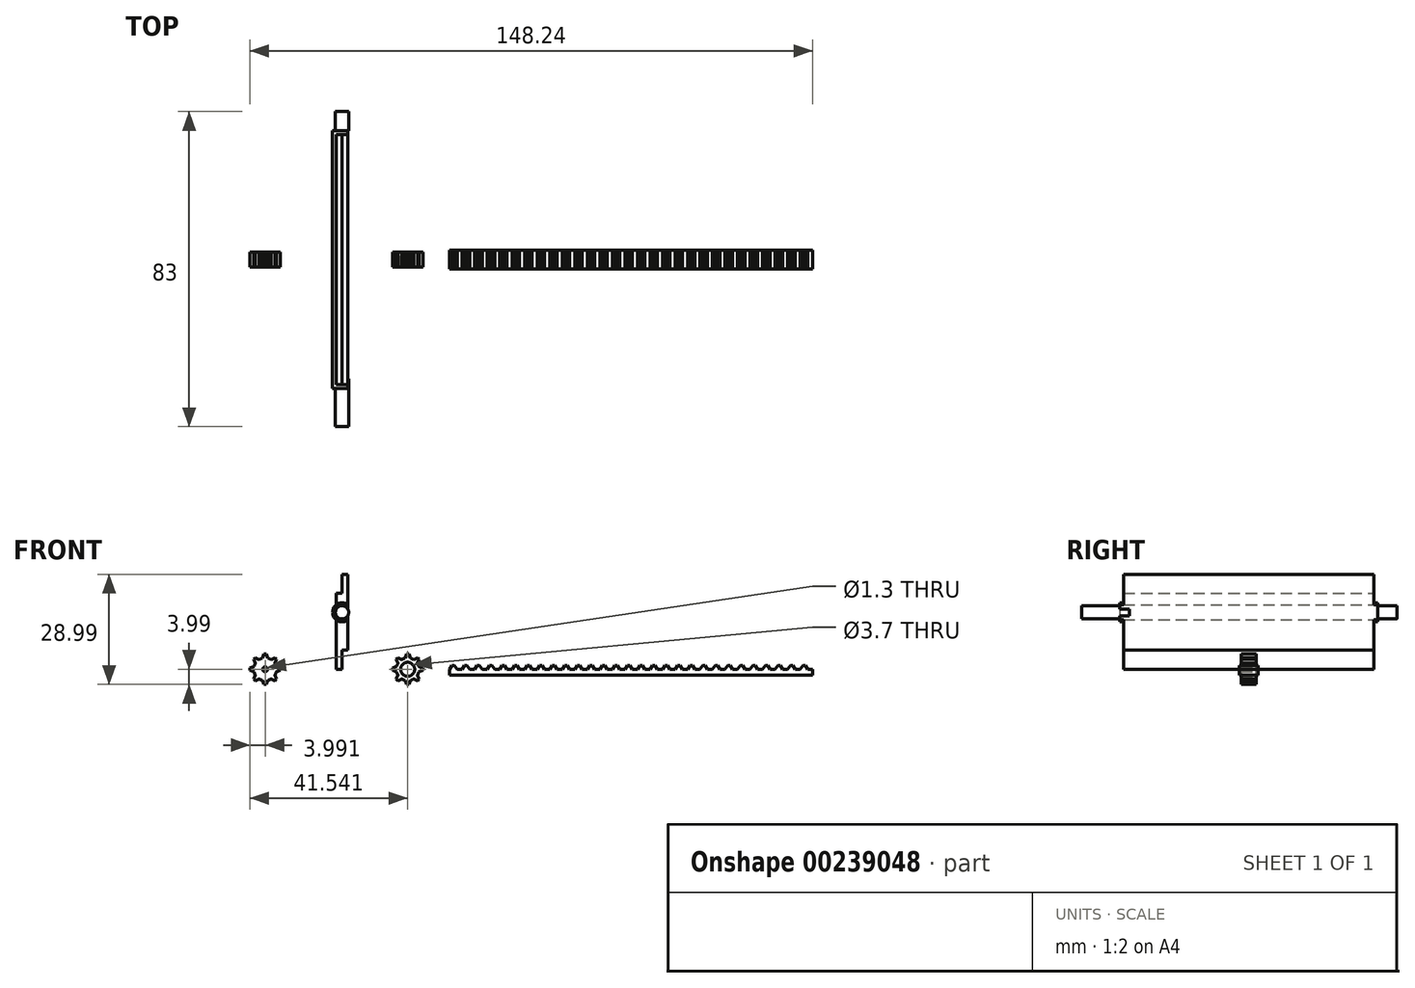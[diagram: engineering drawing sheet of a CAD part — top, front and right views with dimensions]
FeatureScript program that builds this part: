
annotation { "Feature Type Name" : "Feature", "Feature Type Description" : "" }
export const myFeature = defineFeature(function(context is Context, id is Id, definition is map)
    precondition{}
    {
        {
            var Q0;
            Q0=qCreatedBy(makeId("Front.planeOp"),FACE);
            var sketch = newSketch(context, id + "F0", { "sketchPlane" : qUnion([Q0])});
            skLineSegment(sketch, "E0", {"start": v(0, 0) * mm, "end": v(0, 20) * mm});
            skLineSegment(sketch, "E1", {"start": v(0, 20) * mm, "end": v(1.5, 20) * mm});
            skLineSegment(sketch, "E2", {"start": v(1.5, 20) * mm, "end": v(1.5, 25) * mm});
            skLineSegment(sketch, "E3", {"start": v(1.5, 25) * mm, "end": v(3, 25) * mm});
            skLineSegment(sketch, "E4", {"start": v(3, 25) * mm, "end": v(3, 5) * mm});
            skLineSegment(sketch, "E5", {"start": v(3, 5) * mm, "end": v(1.5, 5) * mm});
            skLineSegment(sketch, "E6", {"start": v(1.5, 5) * mm, "end": v(1.5, 0) * mm});
            skLineSegment(sketch, "E7", {"start": v(1.5, 0) * mm, "end": v(0, 0) * mm});
            skCircle(sketch, "E8", {"center": v(1.5, 15) * mm, "radius": 2.5 * mm});
            skSolve(sketch);
        }
        {
            var Q0;
            {var subQ1=sQuery(id+"F0.wireOp",EDGE,"E1");Q0=makeQuery(id+"F0.imprint","IMPRINT",FACE,{"disambiguationData":[TD([[makeQuery(id+"F0.imprint","IMPRINT",EDGE,{"derivedFrom":subQ1}),-1.0]])]});}
            var Q1;
            {var subQ0=sQuery(id+"F0.wireOp",EDGE,"E5");Q1=makeQuery(id+"F0.imprint","IMPRINT",FACE,{"disambiguationData":[TD([[makeQuery(id+"F0.imprint","IMPRINT",EDGE,{"derivedFrom":subQ0}),-1.0]])]});}
            var Q2;
            {var subQ0=sQuery(id+"F0.wireOp",EDGE,"E8");var subQ1=sQuery(id+"F0.wireOp",EDGE,"E0");var subQ2=makeQuery(id+"F0.imprint","INTERSECT",VERTEX,{"disambiguationData":[OD(0.0)],"derivedFrom":[subQ1,subQ0]});Q2=makeQuery(id+"F0.imprint","IMPRINT",FACE,{"disambiguationData":[TD([[makeQuery(id+"F0.imprint","IMPRINT",EDGE,{"disambiguationData":[TD([[subQ2,-1.0]])],"derivedFrom":subQ1}),-1.0]])]});}
            extrude(context, id + "F1", {"entities" : qUnion([Q0, Q1, Q2]), "endBound" : BoundingType.SYMMETRIC, "depth" : 66 * mm});
        }
        {
            var Q0;
            {var subQ0=sQuery(id+"F0.wireOp",EDGE,"E8");var subQ1=sQuery(id+"F0.wireOp",EDGE,"E0");var subQ2=makeQuery(id+"F0.imprint","INTERSECT",VERTEX,{"disambiguationData":[OD(0.0)],"derivedFrom":[subQ1,subQ0]});Q0=makeQuery(id+"F0.imprint","IMPRINT",FACE,{"disambiguationData":[TD([[makeQuery(id+"F0.imprint","IMPRINT",EDGE,{"disambiguationData":[TD([[subQ2,-1.0]])],"derivedFrom":subQ1}),-1.0]])]});}
            var Q1;
            {var subQ0=sQuery(id+"F0.wireOp",EDGE,"E8");var subQ1=sQuery(id+"F0.wireOp",EDGE,"E0");var subQ2=makeQuery(id+"F0.imprint","INTERSECT",VERTEX,{"disambiguationData":[OD(0.0)],"derivedFrom":[subQ1,subQ0]});Q1=makeQuery(id+"F0.imprint","IMPRINT",FACE,{"disambiguationData":[TD([[makeQuery(id+"F0.imprint","IMPRINT",EDGE,{"disambiguationData":[TD([[subQ2,-1.0]])],"derivedFrom":subQ1}),1.0]])]});}
            var Q2;
            {var subQ0=sQuery(id+"F0.wireOp",EDGE,"E8");var subQ1=sQuery(id+"F0.wireOp",EDGE,"E4");var subQ2=makeQuery(id+"F0.imprint","INTERSECT",VERTEX,{"disambiguationData":[OD(0.0)],"derivedFrom":[subQ1,subQ0]});Q2=makeQuery(id+"F0.imprint","IMPRINT",FACE,{"disambiguationData":[TD([[makeQuery(id+"F0.imprint","IMPRINT",EDGE,{"disambiguationData":[TD([[subQ2,-1.0]])],"derivedFrom":subQ1}),1.0]])]});}
            extrude(context, id + "F2", {"entities" : qUnion([Q0, Q1, Q2]), "operationType" : NewBodyOperationType.ADD, "depth" : 34 * mm, "hasSecondDirection" : true, "secondDirectionOppositeDirection" : true, "secondDirectionDepth" : 34 * mm});
        }
        {
            var Q0;
            Q0=makeQuery(id+"F2.opExtrude","CAP_FACE",FACE,{"disambiguationData":[OSD([sQuery(id+"F0.wireOp",EDGE,"E8")])],"isStart":false});
            var sketch = newSketch(context, id + "F3", { "sketchPlane" : qUnion([Q0])});
            skCircle(sketch, "E9", {"center": v(1.5, 15) * mm, "radius": 1.75 * mm});
            skSolve(sketch);
        }
        {
            var Q0;
            Q0 = qSketchRegion(id + "F3", true);
            extrude(context, id + "F4", {"entities" : qUnion([Q0]), "operationType" : NewBodyOperationType.ADD, "depth" : 10 * mm});
        }
        {
            var Q0;
            Q0=makeQuery(id+"F2.opExtrude","CAP_FACE",FACE,{"disambiguationData":[OSD([sQuery(id+"F0.wireOp",EDGE,"E8")])],"isStart":true});
            var sketch = newSketch(context, id + "F5", { "sketchPlane" : qUnion([Q0])});
            skCircle(sketch, "E10", {"center": v(-1.5, 15) * mm, "radius": 1.75 * mm});
            skSolve(sketch);
        }
        {
            var Q0;
            Q0 = qSketchRegion(id + "F5", true);
            extrude(context, id + "F6", {"entities" : qUnion([Q0]), "operationType" : NewBodyOperationType.ADD, "depth" : 5 * mm});
        }
        {
            var Q0;
            Q0=qCreatedBy(makeId("Front.planeOp"),FACE);
            var sketch = newSketch(context, id + "F7", { "sketchPlane" : qUnion([Q0])});
            skCircle(sketch, "E11", {"center": v(18.78, 0) * mm, "radius": 1.85 * mm});
            skArc(sketch, "E12", {"start": v(16.22, 1.57) * mm, "mid": v(16, 1.15) * mm, "end": v(15.86, 0.7) * mm});
            skCircle(sketch, "E13", {"center": v(18.78, 0) * mm, "radius": 4 * mm, "construction": true});
            skLineSegment(sketch, "E14", {"start": v(18.78, 0) * mm, "end": v(18.78, 4) * mm, "construction": true});
            skLineSegment(sketch, "E15", {"start": v(19.08, 3.99) * mm, "end": v(19.48, 2.92) * mm});
            skLineSegment(sketch, "E16.MirrorCS", {"start": v(18.48, 3.99) * mm, "end": v(18.08, 2.92) * mm});
            skLineSegment(sketch, "E17", {"start": v(18.48, 3.99) * mm, "end": v(19.08, 3.99) * mm});
            skLineSegment(sketch, "E18.1.0", {"start": v(21.39, 3.03) * mm, "end": v(20.35, 2.56) * mm});
            skLineSegment(sketch, "E18.1.1", {"start": v(21.39, 3.03) * mm, "end": v(21.81, 2.6) * mm});
            skLineSegment(sketch, "E18.1.2", {"start": v(21.81, 2.6) * mm, "end": v(21.34, 1.57) * mm});
            skLineSegment(sketch, "E18.2.0", {"start": v(22.77, 0.3) * mm, "end": v(21.7, 0.7) * mm});
            skLineSegment(sketch, "E18.2.1", {"start": v(22.77, 0.3) * mm, "end": v(22.77, -0.3) * mm});
            skLineSegment(sketch, "E18.2.2", {"start": v(22.77, -0.3) * mm, "end": v(21.7, -0.7) * mm});
            skLineSegment(sketch, "E18.3.0", {"start": v(21.81, -2.6) * mm, "end": v(21.34, -1.57) * mm});
            skLineSegment(sketch, "E18.3.1", {"start": v(21.81, -2.6) * mm, "end": v(21.39, -3.03) * mm});
            skLineSegment(sketch, "E18.3.2", {"start": v(21.39, -3.03) * mm, "end": v(20.35, -2.56) * mm});
            skLineSegment(sketch, "E18.4.0", {"start": v(19.08, -3.99) * mm, "end": v(19.48, -2.92) * mm});
            skLineSegment(sketch, "E18.4.1", {"start": v(19.08, -3.99) * mm, "end": v(18.48, -3.99) * mm});
            skLineSegment(sketch, "E18.4.2", {"start": v(18.48, -3.99) * mm, "end": v(18.08, -2.92) * mm});
            skLineSegment(sketch, "E18.5.0", {"start": v(16.17, -3.03) * mm, "end": v(17.21, -2.56) * mm});
            skLineSegment(sketch, "E18.5.1", {"start": v(16.17, -3.03) * mm, "end": v(15.75, -2.6) * mm});
            skLineSegment(sketch, "E18.5.2", {"start": v(15.75, -2.6) * mm, "end": v(16.22, -1.57) * mm});
            skLineSegment(sketch, "E18.6.0", {"start": v(14.8, -0.3) * mm, "end": v(15.86, -0.7) * mm});
            skLineSegment(sketch, "E18.6.1", {"start": v(14.8, -0.3) * mm, "end": v(14.8, 0.3) * mm});
            skLineSegment(sketch, "E18.6.2", {"start": v(14.8, 0.3) * mm, "end": v(15.86, 0.7) * mm});
            skLineSegment(sketch, "E18.7.0", {"start": v(15.75, 2.6) * mm, "end": v(16.22, 1.57) * mm});
            skLineSegment(sketch, "E18.7.1", {"start": v(15.75, 2.6) * mm, "end": v(16.17, 3.03) * mm});
            skLineSegment(sketch, "E18.7.2", {"start": v(16.17, 3.03) * mm, "end": v(17.21, 2.56) * mm});
            skLineSegment(sketch, "E18.anchor1", {"start": v(18.78, 0) * mm, "end": v(18.08, 2.92) * mm, "construction": true});
            skLineSegment(sketch, "E18.anchor2", {"start": v(18.78, 0) * mm, "end": v(16.22, 1.57) * mm, "construction": true});
            skLineSegment(sketch, "E19", {"start": v(31.78, 0) * mm, "end": v(31.08, 1) * mm});
            skLineSegment(sketch, "E20", {"start": v(31.08, 1) * mm, "end": v(30.48, 1) * mm});
            skLineSegment(sketch, "E21", {"start": v(30.48, 1) * mm, "end": v(29.78, 0) * mm});
            skLineSegment(sketch, "E22", {"start": v(31.78, 0) * mm, "end": v(33.08, 0) * mm});
            skLineSegment(sketch, "E23.1.0.0", {"start": v(33.78, 1) * mm, "end": v(33.08, 0) * mm});
            skLineSegment(sketch, "E23.1.0.1", {"start": v(34.38, 1) * mm, "end": v(33.78, 1) * mm});
            skLineSegment(sketch, "E23.1.0.2", {"start": v(35.08, 0) * mm, "end": v(34.38, 1) * mm});
            skLineSegment(sketch, "E23.1.0.3", {"start": v(35.08, 0) * mm, "end": v(36.38, 0) * mm});
            skLineSegment(sketch, "E23.2.0.0", {"start": v(37.08, 1) * mm, "end": v(36.38, 0) * mm});
            skLineSegment(sketch, "E23.2.0.1", {"start": v(37.68, 1) * mm, "end": v(37.08, 1) * mm});
            skLineSegment(sketch, "E23.2.0.2", {"start": v(38.38, 0) * mm, "end": v(37.68, 1) * mm});
            skLineSegment(sketch, "E23.2.0.3", {"start": v(38.38, 0) * mm, "end": v(39.68, 0) * mm});
            skLineSegment(sketch, "E23.3.0.0", {"start": v(40.38, 1) * mm, "end": v(39.68, 0) * mm});
            skLineSegment(sketch, "E23.3.0.1", {"start": v(40.98, 1) * mm, "end": v(40.38, 1) * mm});
            skLineSegment(sketch, "E23.3.0.2", {"start": v(41.68, 0) * mm, "end": v(40.98, 1) * mm});
            skLineSegment(sketch, "E23.3.0.3", {"start": v(41.68, 0) * mm, "end": v(42.98, 0) * mm});
            skLineSegment(sketch, "E23.4.0.0", {"start": v(43.68, 1) * mm, "end": v(42.98, 0) * mm});
            skLineSegment(sketch, "E23.4.0.1", {"start": v(44.28, 1) * mm, "end": v(43.68, 1) * mm});
            skLineSegment(sketch, "E23.4.0.2", {"start": v(44.98, 0) * mm, "end": v(44.28, 1) * mm});
            skLineSegment(sketch, "E23.4.0.3", {"start": v(44.98, 0) * mm, "end": v(46.28, 0) * mm});
            skLineSegment(sketch, "E23.5.0.0", {"start": v(46.98, 1) * mm, "end": v(46.28, 0) * mm});
            skLineSegment(sketch, "E23.5.0.1", {"start": v(47.58, 1) * mm, "end": v(46.98, 1) * mm});
            skLineSegment(sketch, "E23.5.0.2", {"start": v(48.28, 0) * mm, "end": v(47.58, 1) * mm});
            skLineSegment(sketch, "E23.5.0.3", {"start": v(48.28, 0) * mm, "end": v(49.58, 0) * mm});
            skLineSegment(sketch, "E23.6.0.0", {"start": v(50.28, 1) * mm, "end": v(49.58, 0) * mm});
            skLineSegment(sketch, "E23.6.0.1", {"start": v(50.88, 1) * mm, "end": v(50.28, 1) * mm});
            skLineSegment(sketch, "E23.6.0.2", {"start": v(51.58, 0) * mm, "end": v(50.88, 1) * mm});
            skLineSegment(sketch, "E23.6.0.3", {"start": v(51.58, 0) * mm, "end": v(52.88, 0) * mm});
            skLineSegment(sketch, "E23.7.0.0", {"start": v(53.58, 1) * mm, "end": v(52.88, 0) * mm});
            skLineSegment(sketch, "E23.7.0.1", {"start": v(54.18, 1) * mm, "end": v(53.58, 1) * mm});
            skLineSegment(sketch, "E23.7.0.2", {"start": v(54.88, 0) * mm, "end": v(54.18, 1) * mm});
            skLineSegment(sketch, "E23.7.0.3", {"start": v(54.88, 0) * mm, "end": v(56.18, 0) * mm});
            skLineSegment(sketch, "E23.8.0.0", {"start": v(56.88, 1) * mm, "end": v(56.18, 0) * mm});
            skLineSegment(sketch, "E23.8.0.1", {"start": v(57.48, 1) * mm, "end": v(56.88, 1) * mm});
            skLineSegment(sketch, "E23.8.0.2", {"start": v(58.18, 0) * mm, "end": v(57.48, 1) * mm});
            skLineSegment(sketch, "E23.8.0.3", {"start": v(58.18, 0) * mm, "end": v(59.48, 0) * mm});
            skLineSegment(sketch, "E23.9.0.0", {"start": v(60.18, 1) * mm, "end": v(59.48, 0) * mm});
            skLineSegment(sketch, "E23.9.0.1", {"start": v(60.78, 1) * mm, "end": v(60.18, 1) * mm});
            skLineSegment(sketch, "E23.9.0.2", {"start": v(61.48, 0) * mm, "end": v(60.78, 1) * mm});
            skLineSegment(sketch, "E23.9.0.3", {"start": v(61.48, 0) * mm, "end": v(62.78, 0) * mm});
            skLineSegment(sketch, "E23.10.0.0", {"start": v(63.48, 1) * mm, "end": v(62.78, 0) * mm});
            skLineSegment(sketch, "E23.10.0.1", {"start": v(64.08, 1) * mm, "end": v(63.48, 1) * mm});
            skLineSegment(sketch, "E23.10.0.2", {"start": v(64.78, 0) * mm, "end": v(64.08, 1) * mm});
            skLineSegment(sketch, "E23.10.0.3", {"start": v(64.78, 0) * mm, "end": v(66.08, 0) * mm});
            skLineSegment(sketch, "E23.11.0.0", {"start": v(66.78, 1) * mm, "end": v(66.08, 0) * mm});
            skLineSegment(sketch, "E23.11.0.1", {"start": v(67.38, 1) * mm, "end": v(66.78, 1) * mm});
            skLineSegment(sketch, "E23.11.0.2", {"start": v(68.08, 0) * mm, "end": v(67.38, 1) * mm});
            skLineSegment(sketch, "E23.11.0.3", {"start": v(68.08, 0) * mm, "end": v(69.38, 0) * mm});
            skLineSegment(sketch, "E23.12.0.0", {"start": v(70.08, 1) * mm, "end": v(69.38, 0) * mm});
            skLineSegment(sketch, "E23.12.0.1", {"start": v(70.68, 1) * mm, "end": v(70.08, 1) * mm});
            skLineSegment(sketch, "E23.12.0.2", {"start": v(71.38, 0) * mm, "end": v(70.68, 1) * mm});
            skLineSegment(sketch, "E23.12.0.3", {"start": v(71.38, 0) * mm, "end": v(72.68, 0) * mm});
            skLineSegment(sketch, "E23.13.0.0", {"start": v(73.38, 1) * mm, "end": v(72.68, 0) * mm});
            skLineSegment(sketch, "E23.13.0.1", {"start": v(73.98, 1) * mm, "end": v(73.38, 1) * mm});
            skLineSegment(sketch, "E23.13.0.2", {"start": v(74.68, 0) * mm, "end": v(73.98, 1) * mm});
            skLineSegment(sketch, "E23.13.0.3", {"start": v(74.68, 0) * mm, "end": v(75.98, 0) * mm});
            skLineSegment(sketch, "E23.14.0.0", {"start": v(76.68, 1) * mm, "end": v(75.98, 0) * mm});
            skLineSegment(sketch, "E23.14.0.1", {"start": v(77.28, 1) * mm, "end": v(76.68, 1) * mm});
            skLineSegment(sketch, "E23.14.0.2", {"start": v(77.98, 0) * mm, "end": v(77.28, 1) * mm});
            skLineSegment(sketch, "E23.14.0.3", {"start": v(77.98, 0) * mm, "end": v(79.28, 0) * mm});
            skLineSegment(sketch, "E23.15.0.0", {"start": v(79.98, 1) * mm, "end": v(79.28, 0) * mm});
            skLineSegment(sketch, "E23.15.0.1", {"start": v(80.58, 1) * mm, "end": v(79.98, 1) * mm});
            skLineSegment(sketch, "E23.15.0.2", {"start": v(81.28, 0) * mm, "end": v(80.58, 1) * mm});
            skLineSegment(sketch, "E23.15.0.3", {"start": v(81.28, 0) * mm, "end": v(82.58, 0) * mm});
            skLineSegment(sketch, "E23.16.0.0", {"start": v(83.28, 1) * mm, "end": v(82.58, 0) * mm});
            skLineSegment(sketch, "E23.16.0.1", {"start": v(83.88, 1) * mm, "end": v(83.28, 1) * mm});
            skLineSegment(sketch, "E23.16.0.2", {"start": v(84.58, 0) * mm, "end": v(83.88, 1) * mm});
            skLineSegment(sketch, "E23.16.0.3", {"start": v(84.58, 0) * mm, "end": v(85.88, 0) * mm});
            skLineSegment(sketch, "E23.17.0.0", {"start": v(86.58, 1) * mm, "end": v(85.88, 0) * mm});
            skLineSegment(sketch, "E23.17.0.1", {"start": v(87.18, 1) * mm, "end": v(86.58, 1) * mm});
            skLineSegment(sketch, "E23.17.0.2", {"start": v(87.88, 0) * mm, "end": v(87.18, 1) * mm});
            skLineSegment(sketch, "E23.17.0.3", {"start": v(87.88, 0) * mm, "end": v(89.18, 0) * mm});
            skLineSegment(sketch, "E23.18.0.0", {"start": v(89.88, 1) * mm, "end": v(89.18, 0) * mm});
            skLineSegment(sketch, "E23.18.0.1", {"start": v(90.48, 1) * mm, "end": v(89.88, 1) * mm});
            skLineSegment(sketch, "E23.18.0.2", {"start": v(91.18, 0) * mm, "end": v(90.48, 1) * mm});
            skLineSegment(sketch, "E23.18.0.3", {"start": v(91.18, 0) * mm, "end": v(92.48, 0) * mm});
            skLineSegment(sketch, "E23.19.0.0", {"start": v(93.18, 1) * mm, "end": v(92.48, 0) * mm});
            skLineSegment(sketch, "E23.19.0.1", {"start": v(93.78, 1) * mm, "end": v(93.18, 1) * mm});
            skLineSegment(sketch, "E23.19.0.2", {"start": v(94.48, 0) * mm, "end": v(93.78, 1) * mm});
            skLineSegment(sketch, "E23.19.0.3", {"start": v(94.48, 0) * mm, "end": v(95.78, 0) * mm});
            skLineSegment(sketch, "E23.20.0.0", {"start": v(96.48, 1) * mm, "end": v(95.78, 0) * mm});
            skLineSegment(sketch, "E23.20.0.1", {"start": v(97.08, 1) * mm, "end": v(96.48, 1) * mm});
            skLineSegment(sketch, "E23.20.0.2", {"start": v(97.78, 0) * mm, "end": v(97.08, 1) * mm});
            skLineSegment(sketch, "E23.20.0.3", {"start": v(97.78, 0) * mm, "end": v(99.08, 0) * mm});
            skLineSegment(sketch, "E23.21.0.0", {"start": v(99.78, 1) * mm, "end": v(99.08, 0) * mm});
            skLineSegment(sketch, "E23.21.0.1", {"start": v(100.38, 1) * mm, "end": v(99.78, 1) * mm});
            skLineSegment(sketch, "E23.21.0.2", {"start": v(101.08, 0) * mm, "end": v(100.38, 1) * mm});
            skLineSegment(sketch, "E23.21.0.3", {"start": v(101.08, 0) * mm, "end": v(102.38, 0) * mm});
            skLineSegment(sketch, "E23.22.0.0", {"start": v(103.08, 1) * mm, "end": v(102.38, 0) * mm});
            skLineSegment(sketch, "E23.22.0.1", {"start": v(103.68, 1) * mm, "end": v(103.08, 1) * mm});
            skLineSegment(sketch, "E23.22.0.2", {"start": v(104.38, 0) * mm, "end": v(103.68, 1) * mm});
            skLineSegment(sketch, "E23.22.0.3", {"start": v(104.38, 0) * mm, "end": v(105.68, 0) * mm});
            skLineSegment(sketch, "E23.23.0.0", {"start": v(106.38, 1) * mm, "end": v(105.68, 0) * mm});
            skLineSegment(sketch, "E23.23.0.1", {"start": v(106.98, 1) * mm, "end": v(106.38, 1) * mm});
            skLineSegment(sketch, "E23.23.0.2", {"start": v(107.68, 0) * mm, "end": v(106.98, 1) * mm});
            skLineSegment(sketch, "E23.23.0.3", {"start": v(107.68, 0) * mm, "end": v(108.98, 0) * mm});
            skLineSegment(sketch, "E23.24.0.0", {"start": v(109.68, 1) * mm, "end": v(108.98, 0) * mm});
            skLineSegment(sketch, "E23.24.0.1", {"start": v(110.28, 1) * mm, "end": v(109.68, 1) * mm});
            skLineSegment(sketch, "E23.24.0.2", {"start": v(110.98, 0) * mm, "end": v(110.28, 1) * mm});
            skLineSegment(sketch, "E23.24.0.3", {"start": v(110.98, 0) * mm, "end": v(112.28, 0) * mm});
            skLineSegment(sketch, "E23.25.0.0", {"start": v(112.98, 1) * mm, "end": v(112.28, 0) * mm});
            skLineSegment(sketch, "E23.25.0.1", {"start": v(113.58, 1) * mm, "end": v(112.98, 1) * mm});
            skLineSegment(sketch, "E23.25.0.2", {"start": v(114.28, 0) * mm, "end": v(113.58, 1) * mm});
            skLineSegment(sketch, "E23.25.0.3", {"start": v(114.28, 0) * mm, "end": v(115.58, 0) * mm});
            skLineSegment(sketch, "E23.26.0.0", {"start": v(116.28, 1) * mm, "end": v(115.58, 0) * mm});
            skLineSegment(sketch, "E23.26.0.1", {"start": v(116.88, 1) * mm, "end": v(116.28, 1) * mm});
            skLineSegment(sketch, "E23.26.0.2", {"start": v(117.58, 0) * mm, "end": v(116.88, 1) * mm});
            skLineSegment(sketch, "E23.26.0.3", {"start": v(117.58, 0) * mm, "end": v(118.88, 0) * mm});
            skLineSegment(sketch, "E23.27.0.0", {"start": v(119.58, 1) * mm, "end": v(118.88, 0) * mm});
            skLineSegment(sketch, "E23.27.0.1", {"start": v(120.18, 1) * mm, "end": v(119.58, 1) * mm});
            skLineSegment(sketch, "E23.27.0.2", {"start": v(120.88, 0) * mm, "end": v(120.18, 1) * mm});
            skLineSegment(sketch, "E23.27.0.3", {"start": v(120.88, 0) * mm, "end": v(122.18, 0) * mm});
            skLineSegment(sketch, "E23.28.0.0", {"start": v(122.88, 1) * mm, "end": v(122.18, 0) * mm});
            skLineSegment(sketch, "E23.28.0.1", {"start": v(123.48, 1) * mm, "end": v(122.88, 1) * mm});
            skLineSegment(sketch, "E23.28.0.2", {"start": v(124.18, 0) * mm, "end": v(123.48, 1) * mm});
            skLineSegment(sketch, "E23.28.0.3", {"start": v(124.18, 0) * mm, "end": v(125.48, 0) * mm});
            skLineSegment(sketch, "E23.direction1", {"start": v(29.78, 0) * mm, "end": v(33.08, 0) * mm, "construction": true});
            skLineSegment(sketch, "E24", {"start": v(29.78, 0) * mm, "end": v(29.78, -1.5) * mm});
            skLineSegment(sketch, "E25", {"start": v(29.78, -1.5) * mm, "end": v(125.48, -1.5) * mm});
            skLineSegment(sketch, "E26", {"start": v(125.48, -1.5) * mm, "end": v(125.48, 0) * mm});
            skArc(sketch, "E27.trimOffspring", {"start": v(15.86, -0.7) * mm, "mid": v(16, -1.15) * mm, "end": v(16.22, -1.57) * mm});
            skArc(sketch, "E28.trimOffspring", {"start": v(18.08, 2.92) * mm, "mid": v(17.63, 2.77) * mm, "end": v(17.21, 2.56) * mm});
            skArc(sketch, "E29.trimOffspring", {"start": v(20.35, 2.56) * mm, "mid": v(19.93, 2.77) * mm, "end": v(19.48, 2.92) * mm});
            skArc(sketch, "E30.trimOffspring", {"start": v(21.7, 0.7) * mm, "mid": v(21.55, 1.15) * mm, "end": v(21.34, 1.57) * mm});
            skArc(sketch, "E31.trimOffspring", {"start": v(21.34, -1.57) * mm, "mid": v(21.55, -1.15) * mm, "end": v(21.7, -0.7) * mm});
            skArc(sketch, "E32.trimOffspring", {"start": v(19.48, -2.92) * mm, "mid": v(19.93, -2.77) * mm, "end": v(20.35, -2.56) * mm});
            skArc(sketch, "E33.trimOffspring", {"start": v(17.21, -2.56) * mm, "mid": v(17.63, -2.77) * mm, "end": v(18.08, -2.92) * mm});
            skCircle(sketch, "E34", {"center": v(-18.77, 0) * mm, "radius": 0.65 * mm});
            skArc(sketch, "E35", {"start": v(-21.33, 1.57) * mm, "mid": v(-21.54, 1.15) * mm, "end": v(-21.69, 0.7) * mm});
            skCircle(sketch, "E36", {"center": v(-18.77, 0) * mm, "radius": 4 * mm, "construction": true});
            skLineSegment(sketch, "E37", {"start": v(-18.77, 0) * mm, "end": v(-18.77, 4) * mm, "construction": true});
            skLineSegment(sketch, "E38", {"start": v(-18.47, 3.99) * mm, "end": v(-18.07, 2.92) * mm});
            skLineSegment(sketch, "E39.MirrorCS", {"start": v(-19.07, 3.99) * mm, "end": v(-19.47, 2.92) * mm});
            skLineSegment(sketch, "E40", {"start": v(-19.07, 3.99) * mm, "end": v(-18.47, 3.99) * mm});
            skLineSegment(sketch, "E41.1.0", {"start": v(-16.16, 3.03) * mm, "end": v(-17.2, 2.56) * mm});
            skLineSegment(sketch, "E41.1.1", {"start": v(-16.16, 3.03) * mm, "end": v(-15.74, 2.6) * mm});
            skLineSegment(sketch, "E41.1.2", {"start": v(-15.74, 2.6) * mm, "end": v(-16.21, 1.57) * mm});
            skLineSegment(sketch, "E41.2.0", {"start": v(-14.78, 0.3) * mm, "end": v(-15.85, 0.7) * mm});
            skLineSegment(sketch, "E41.2.1", {"start": v(-14.78, 0.3) * mm, "end": v(-14.78, -0.3) * mm});
            skLineSegment(sketch, "E41.2.2", {"start": v(-14.78, -0.3) * mm, "end": v(-15.85, -0.7) * mm});
            skLineSegment(sketch, "E41.3.0", {"start": v(-15.74, -2.6) * mm, "end": v(-16.21, -1.57) * mm});
            skLineSegment(sketch, "E41.3.1", {"start": v(-15.74, -2.6) * mm, "end": v(-16.16, -3.03) * mm});
            skLineSegment(sketch, "E41.3.2", {"start": v(-16.16, -3.03) * mm, "end": v(-17.2, -2.56) * mm});
            skLineSegment(sketch, "E41.4.0", {"start": v(-18.47, -3.99) * mm, "end": v(-18.07, -2.92) * mm});
            skLineSegment(sketch, "E41.4.1", {"start": v(-18.47, -3.99) * mm, "end": v(-19.07, -3.99) * mm});
            skLineSegment(sketch, "E41.4.2", {"start": v(-19.07, -3.99) * mm, "end": v(-19.47, -2.92) * mm});
            skLineSegment(sketch, "E41.5.0", {"start": v(-21.38, -3.03) * mm, "end": v(-20.34, -2.56) * mm});
            skLineSegment(sketch, "E41.5.1", {"start": v(-21.38, -3.03) * mm, "end": v(-21.8, -2.6) * mm});
            skLineSegment(sketch, "E41.5.2", {"start": v(-21.8, -2.6) * mm, "end": v(-21.33, -1.57) * mm});
            skLineSegment(sketch, "E41.6.0", {"start": v(-22.76, -0.3) * mm, "end": v(-21.69, -0.7) * mm});
            skLineSegment(sketch, "E41.6.1", {"start": v(-22.76, -0.3) * mm, "end": v(-22.76, 0.3) * mm});
            skLineSegment(sketch, "E41.6.2", {"start": v(-22.76, 0.3) * mm, "end": v(-21.69, 0.7) * mm});
            skLineSegment(sketch, "E41.7.0", {"start": v(-21.8, 2.6) * mm, "end": v(-21.33, 1.57) * mm});
            skLineSegment(sketch, "E41.7.1", {"start": v(-21.8, 2.6) * mm, "end": v(-21.38, 3.03) * mm});
            skLineSegment(sketch, "E41.7.2", {"start": v(-21.38, 3.03) * mm, "end": v(-20.34, 2.56) * mm});
            skLineSegment(sketch, "E41.anchor1", {"start": v(-18.77, 0) * mm, "end": v(-19.47, 2.92) * mm, "construction": true});
            skLineSegment(sketch, "E41.anchor2", {"start": v(-18.77, 0) * mm, "end": v(-21.33, 1.57) * mm, "construction": true});
            skArc(sketch, "E42.trimOffspring", {"start": v(-21.69, -0.7) * mm, "mid": v(-21.54, -1.15) * mm, "end": v(-21.33, -1.57) * mm});
            skArc(sketch, "E43.trimOffspring", {"start": v(-19.47, 2.92) * mm, "mid": v(-19.92, 2.77) * mm, "end": v(-20.34, 2.56) * mm});
            skArc(sketch, "E44.trimOffspring", {"start": v(-17.2, 2.56) * mm, "mid": v(-17.62, 2.77) * mm, "end": v(-18.07, 2.92) * mm});
            skArc(sketch, "E45.trimOffspring", {"start": v(-15.85, 0.7) * mm, "mid": v(-16, 1.15) * mm, "end": v(-16.21, 1.57) * mm});
            skArc(sketch, "E46.trimOffspring", {"start": v(-16.21, -1.57) * mm, "mid": v(-16, -1.15) * mm, "end": v(-15.85, -0.7) * mm});
            skArc(sketch, "E47.trimOffspring", {"start": v(-18.07, -2.92) * mm, "mid": v(-17.62, -2.77) * mm, "end": v(-17.2, -2.56) * mm});
            skArc(sketch, "E48.trimOffspring", {"start": v(-20.34, -2.56) * mm, "mid": v(-19.92, -2.77) * mm, "end": v(-19.47, -2.92) * mm});
            skSolve(sketch);
        }
        {
            var Q0;
            Q0=makeQuery(id+"F7.imprint","IMPRINT",FACE,{"disambiguationData":[TD([[makeQuery(id+"F7.imprint","IMPRINT",EDGE,{"derivedFrom":sQuery(id+"F7.wireOp",EDGE,"E34")}),-1.0]])]});
            extrude(context, id + "F8", {"entities" : qUnion([Q0]), "endBound" : BoundingType.SYMMETRIC, "depth" : 4 * mm});
        }
        {
            var Q0;
            Q0=makeQuery(id+"F7.imprint","IMPRINT",FACE,{"disambiguationData":[TD([[makeQuery(id+"F7.imprint","IMPRINT",EDGE,{"derivedFrom":sQuery(id+"F7.wireOp",EDGE,"E11")}),-1.0]])]});
            extrude(context, id + "F9", {"entities" : qUnion([Q0]), "endBound" : BoundingType.SYMMETRIC, "depth" : 4 * mm});
        }
        {
            var Q0;
            Q0 = qSketchRegion(id + "F3", true);
            var Q1;
            Q1=makeQuery(id+"F7.imprint","IMPRINT",FACE,{"disambiguationData":[TD([[makeQuery(id+"F7.imprint","IMPRINT",EDGE,{"derivedFrom":sQuery(id+"F7.wireOp",EDGE,"E19")}),1.0]])]});
            extrude(context, id + "F10", {"entities" : qUnion([Q0, Q1]), "operationType" : NewBodyOperationType.ADD, "endBound" : BoundingType.SYMMETRIC, "depth" : 5 * mm});
        }
    });
